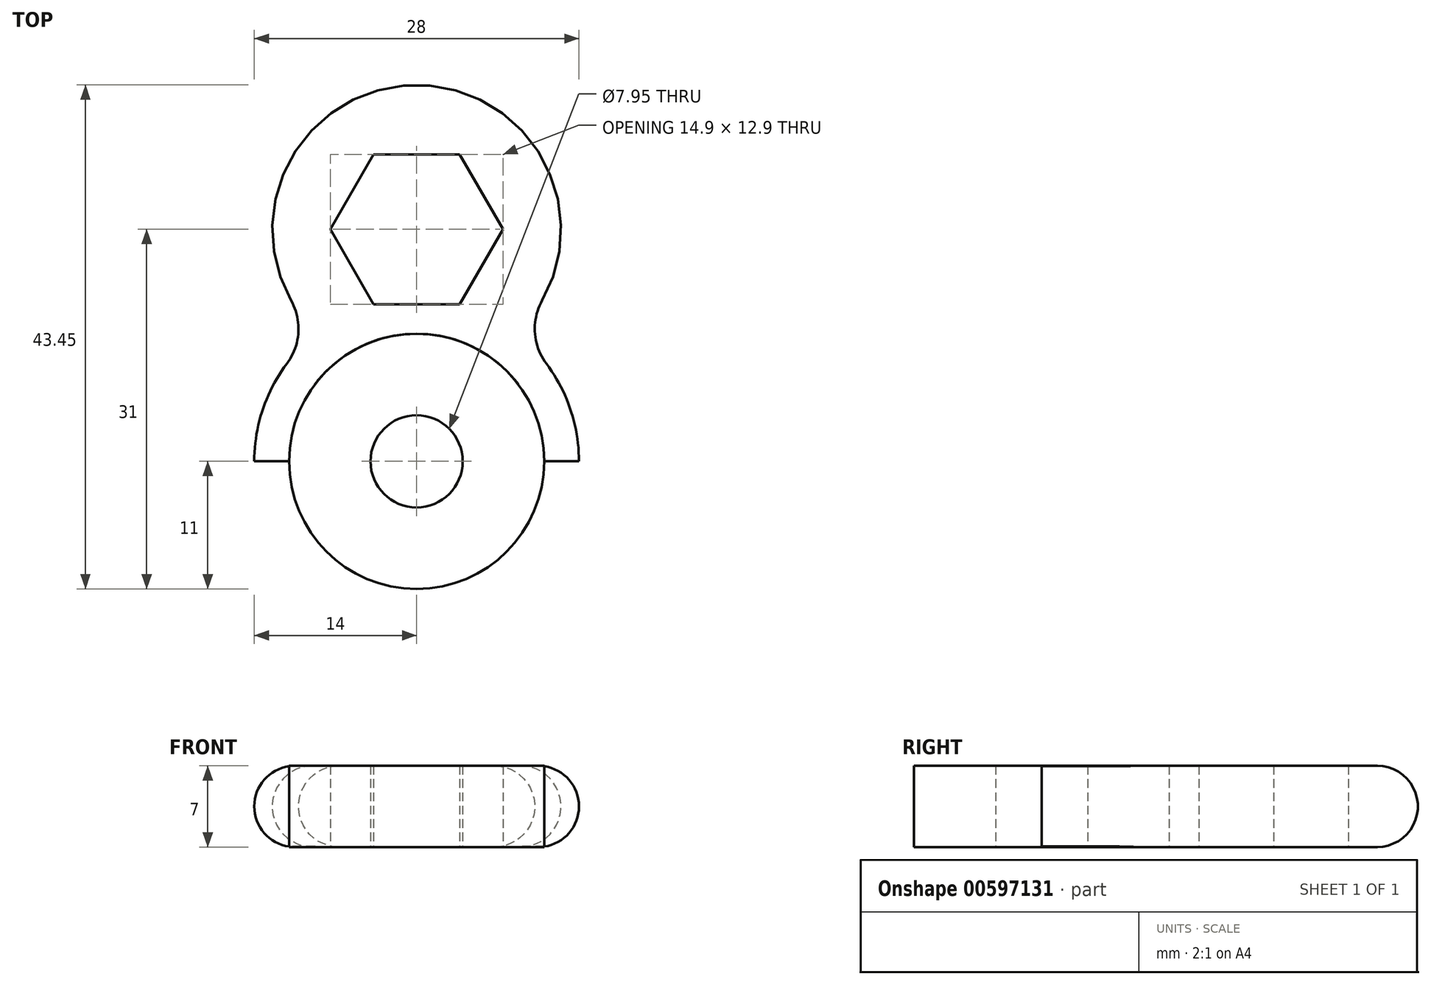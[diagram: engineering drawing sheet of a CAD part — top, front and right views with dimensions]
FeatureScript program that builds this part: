
annotation { "Feature Type Name" : "Feature", "Feature Type Description" : "" }
export const myFeature = defineFeature(function(context is Context, id is Id, definition is map)
    precondition{}
    {
        {
            var Q0;
            Q0=qCreatedBy(makeId("Top.planeOp"),FACE);
            var sketch = newSketch(context, id + "F0", { "sketchPlane" : qUnion([Q0])});
            skCircle(sketch, "E0", {"center": v(0, 0) * mm, "radius": 11 * mm});
            skCircle(sketch, "E1", {"center": v(0, 0) * mm, "radius": 3.98 * mm});
            skSolve(sketch);
        }
        {
            var Q0;
            Q0=qSketchRegion(id+"F0",true);
            extrude(context, id + "F1", {"entities" : qUnion([Q0]), "depth" : 7 * mm, "offsetDistance" : 25 * mm});
        }
        {
            var Q0;
            Q0=qCreatedBy(makeId("Top.planeOp"),FACE);
            var sketch = newSketch(context, id + "F2", { "sketchPlane" : qUnion([Q0])});
            skArc(sketch, "E2", {"start": v(11, 0) * mm, "mid": v(0, 11) * mm, "end": v(-11, 0) * mm});
            skArc(sketch, "E3", {"start": v(-11.2, 8.41) * mm, "mid": v(-13.28, 4.43) * mm, "end": v(-14, 0) * mm});
            skArc(sketch, "E4", {"start": v(-10.84, 13.87) * mm, "mid": v(-10.2, 11.09) * mm, "end": v(-11.2, 8.41) * mm});
            skLineSegment(sketch, "E5", {"start": v(-30.04, 11.09) * mm, "end": v(37.88, 11.09) * mm, "construction": true});
            skPoint(sketch, "E5.startSnap0", {"position": v(-10.2, 11.09) * mm});
            skArc(sketch, "E6.MirrorCS", {"start": v(10.84, 13.87) * mm, "mid": v(10.2, 11.09) * mm, "end": v(11.2, 8.41) * mm});
            skCircle(sketch, "E7.cCircle", {"center": v(0, 20) * mm, "radius": 6.45 * mm, "construction": true});
            skLineSegment(sketch, "E7.0", {"start": v(3.72, 26.45) * mm, "end": v(7.45, 20) * mm});
            skLineSegment(sketch, "E7.1", {"start": v(7.45, 20) * mm, "end": v(3.72, 13.55) * mm});
            skLineSegment(sketch, "E7.2", {"start": v(3.72, 13.55) * mm, "end": v(-3.72, 13.55) * mm});
            skLineSegment(sketch, "E7.3", {"start": v(-3.72, 13.55) * mm, "end": v(-7.45, 20) * mm});
            skLineSegment(sketch, "E7.4", {"start": v(-7.45, 20) * mm, "end": v(-3.72, 26.45) * mm});
            skLineSegment(sketch, "E7.5", {"start": v(-3.72, 26.45) * mm, "end": v(3.72, 26.45) * mm});
            skPoint(sketch, "E7.0.midPoint", {"position": v(5.59, 23.23) * mm});
            skArc(sketch, "E8", {"start": v(-10.84, 13.87) * mm, "mid": v(0, 32.45) * mm, "end": v(10.84, 13.87) * mm});
            skLineSegment(sketch, "E9", {"start": v(14, 0) * mm, "end": v(11, 0) * mm});
            skLineSegment(sketch, "E10", {"start": v(-14, 0) * mm, "end": v(-11, 0) * mm});
            skArc(sketch, "E11.trimOffspring", {"start": v(14, 0) * mm, "mid": v(13.28, 4.43) * mm, "end": v(11.2, 8.41) * mm});
            skSolve(sketch);
        }
        {
            var Q0;
            Q0=qSketchRegion(id+"F2",true);
            extrude(context, id + "F3", {"entities" : qUnion([Q0]), "depth" : 7 * mm, "offsetDistance" : 25 * mm});
        }
        {
            var Q0;
            Q0=qCreatedBy(makeId("Front.planeOp"),FACE);
            var sketch = newSketch(context, id + "F4", { "sketchPlane" : qUnion([Q0])});
            skLineSegment(sketch, "E12", {"start": v(0, 0) * mm, "end": v(0, 44.84) * mm, "construction": true});
            skSolve(sketch);
        }
        {
            var Q0;
            Q0=makeQuery(id+"F3.opExtrude","CAP_EDGE",EDGE,{"disambiguationData":[OSD([sQuery(id+"F2.wireOp",EDGE,"E4")])],"isStart":true});
            var Q1;
            Q1=makeQuery(id+"F3.opExtrude","CAP_EDGE",EDGE,{"disambiguationData":[OSD([sQuery(id+"F2.wireOp",EDGE,"E4")])],"isStart":false});
            fillet(context, id + "F5", {"entities" : qUnion([Q0, Q1]), "radius" : 3.5 * mm, "tangentPropagation" : true, "allowEdgeOverflow" : false});
        }
    });
